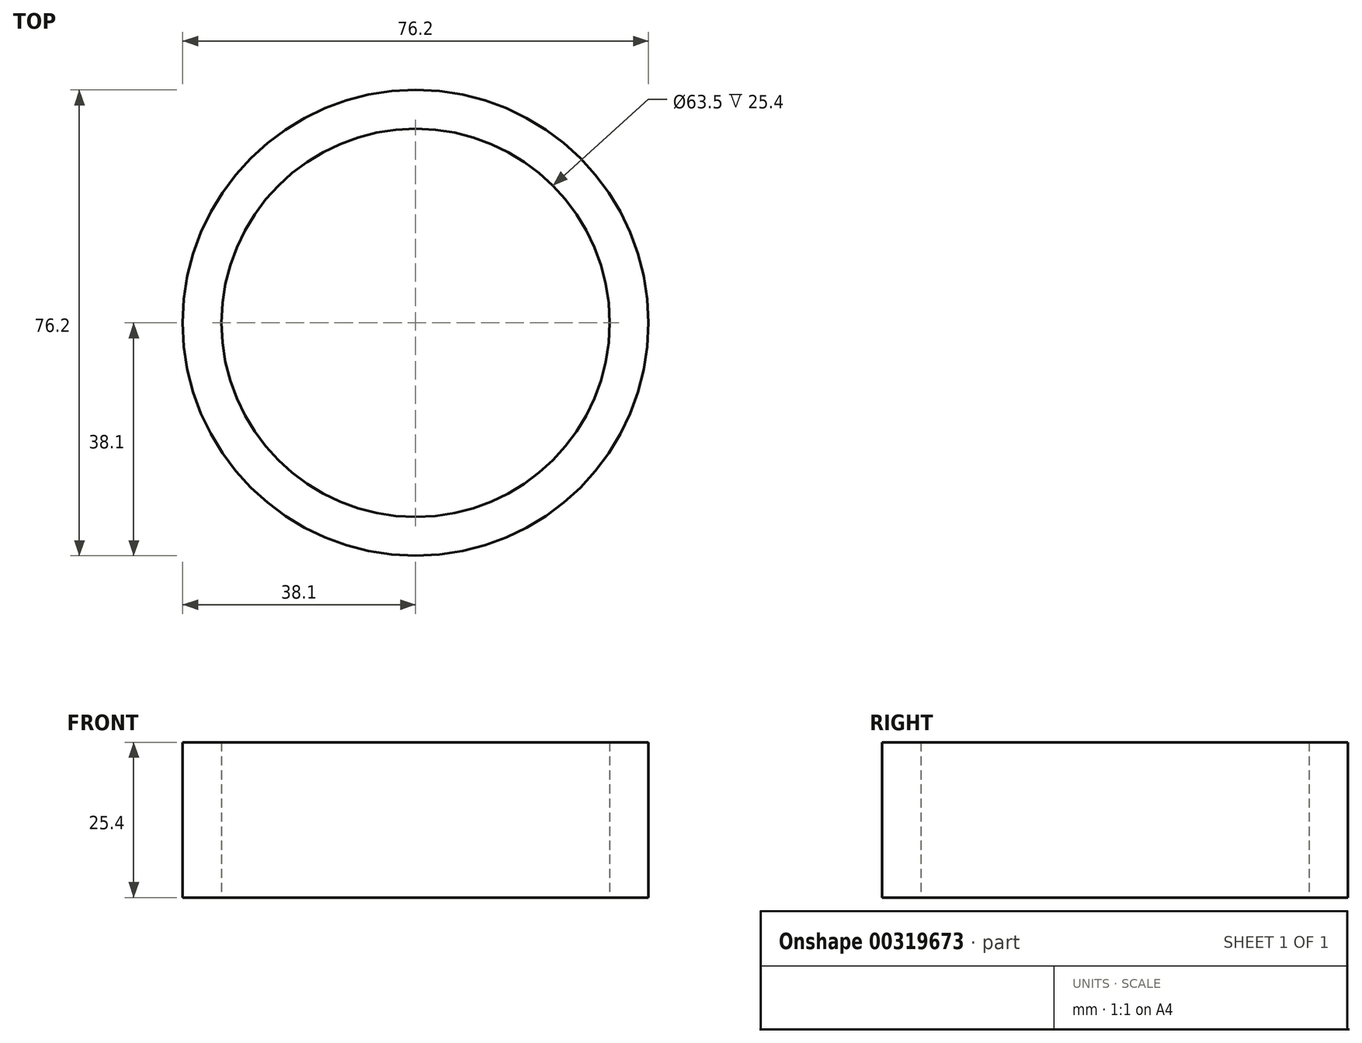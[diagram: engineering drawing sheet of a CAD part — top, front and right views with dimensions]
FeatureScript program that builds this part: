
annotation { "Feature Type Name" : "Feature", "Feature Type Description" : "" }
export const myFeature = defineFeature(function(context is Context, id is Id, definition is map)
    precondition{}
    {
        {
            var Q0;
            Q0=qCreatedBy(makeId("Top.planeOp"),FACE);
            var sketch = newSketch(context, id + "F0", { "sketchPlane" : qUnion([Q0])});
            skCircle(sketch, "E0", {"center": v(0, 0) * mm, "radius": 38.1 * mm});
            skCircle(sketch, "E1", {"center": v(0, 0) * mm, "radius": 31.75 * mm});
            skSolve(sketch);
        }
        {
            var Q0;
            Q0=makeQuery(id+"F0.imprint","IMPRINT",FACE,{"disambiguationData":[TD([[makeQuery(id+"F0.imprint","IMPRINT",EDGE,{"derivedFrom":sQuery(id+"F0.wireOp",EDGE,"E0")}),1.0]])]});
            extrude(context, id + "F1", {"entities" : qUnion([Q0]), "depth" : 25.4 * mm});
        }
    });
